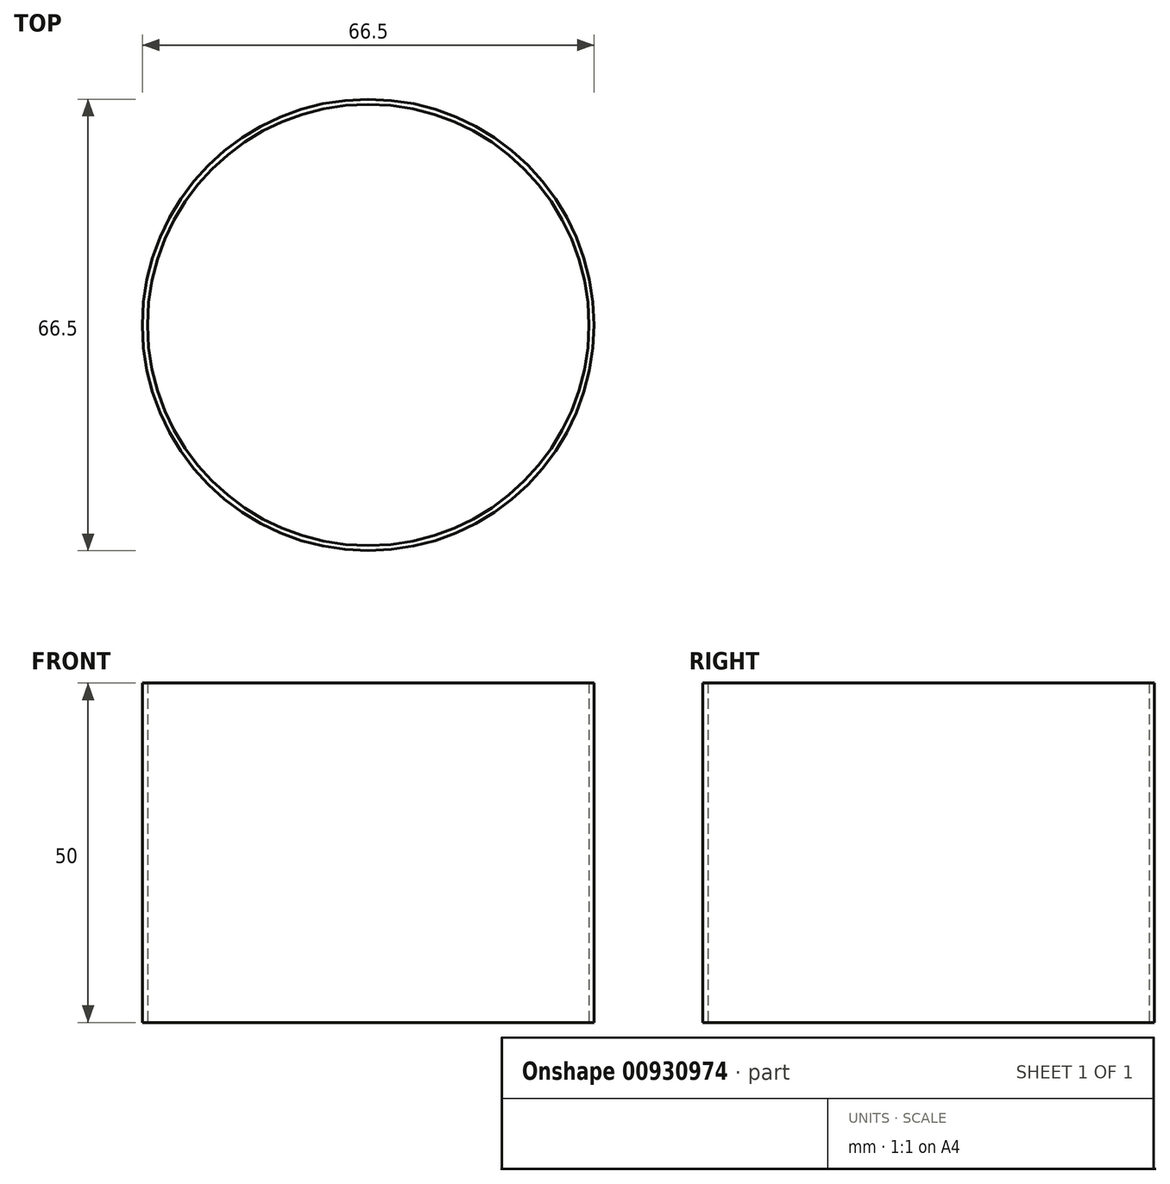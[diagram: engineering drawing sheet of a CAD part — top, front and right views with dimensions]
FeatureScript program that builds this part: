
annotation { "Feature Type Name" : "Feature", "Feature Type Description" : "" }
export const myFeature = defineFeature(function(context is Context, id is Id, definition is map)
    precondition{}
    {
        {
            var Q0;
            Q0=qCreatedBy(makeId("Top.planeOp"),FACE);
            var sketch = newSketch(context, id + "F0", { "sketchPlane" : qUnion([Q0])});
            skCircle(sketch, "E0", {"center": v(0, 0) * mm, "radius": 32.5 * mm});
            skCircle(sketch, "E1", {"center": v(0, 0) * mm, "radius": 33.25 * mm});
            skSolve(sketch);
        }
        {
            var Q0;
            Q0=makeQuery(id+"F0.imprint","IMPRINT",FACE,{"disambiguationData":[TD([[makeQuery(id+"F0.imprint","IMPRINT",EDGE,{"derivedFrom":sQuery(id+"F0.wireOp",EDGE,"E0")}),-1.0]])]});
            extrude(context, id + "F1", {"entities" : qUnion([Q0]), "depth" : 50 * mm, "offsetDistance" : 25 * mm});
        }
    });
